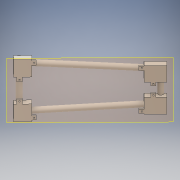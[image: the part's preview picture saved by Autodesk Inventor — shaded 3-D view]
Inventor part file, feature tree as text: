
AUTODESK INVENTOR PART (.ipt)
format: ipt  version: 2019.3 (Build 233278000, 278)  size: 340,992 bytes
history: native  units: mm
features: other x9, extrude x4, thicken_offset x4, sketch x3, plane x2, boolean_combine x2, delete_face x2, mirror x1
ambient origin geometry x8: Origin, YZ Plane, XZ Plane, XY Plane, X Axis, Y Axis, Z Axis, Center Point
bodies: Solid1 (feature_tree)
feature tree (27):
  other  "LowerCage.ipt"
  plane  "Work Plane8"
  sketch  "Sketch1"  dims[d0=10.0mm d1=16.5mm]
  extrude  "Extrusion1"  Depth=10.0mm
  extrude  "Extrusion3"  Depth=4.0mm
  sketch  "Sketch2"  dims[d2=16.0mm d3=0.0mm d4=4.0mm d5=4.0mm d6=4.0mm d7=4.0mm d8=4.0mm d9=0.0mm d10=16.0mm d11=0.0mm d12=4.0mm d13=0.0mm d14=0.25mm d15=0.25mm d16=0.25mm d17=0.25mm d18=0.25mm d19=0.25mm d20=0.25mm d21=0.25mm]
  extrude  "Extrusion2"  Depth=4.0mm
  extrude  "Extrusion4"  Depth=4.0mm
  boolean_combine  "Combine2"
  delete_face  "Delete Face2"
  boolean_combine  "Combine3"
  delete_face  "Delete Face3"
  mirror  "Mirror1"
  thicken_offset  "Thicken1"
  thicken_offset  "Thicken2"
  thicken_offset  "Thicken3"
  thicken_offset  "Thicken4"
  other  "BaseCage::LowerCage.ipt"
  other  "TaggingFeature1"
  sketch  "3D Sketch1"
  plane  "Work Plane1"
  other  "JigPartARight"
  other  "JigPartBRight"
  other  "Pattern of JigPartBRight:1"
  other  "JigPartALeft"
  other  "Pattern of JigPartBRight:2"
  other  "JigPartBLeft"
